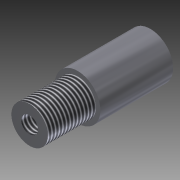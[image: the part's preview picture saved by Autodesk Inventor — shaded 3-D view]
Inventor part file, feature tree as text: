
AUTODESK INVENTOR PART (.ipt)
format: ipt  version: 2012 (Build 160160000, 160)  size: 96,768 bytes
history: native  units: in
note: dims shown in document units (in); Inventor stores cm internally (conversion verified against a paired STEP export)
features: extrude x3, sketch x2, thread x2
ambient origin geometry x8: Origin, YZ Plane, XZ Plane, XY Plane, X Axis, Y Axis, Z Axis, Center Point
bodies: Solid1 (feature_tree)
feature tree (7):
  sketch  "Sketch1"  dims[d0=0.625in d1=0.5in]
  extrude  "Extrusion1"  Depth=0.5in
  extrude  "Extrusion2"  Depth=0.66in TaperAngle=0.0deg
  thread  "Thread1"  [1 undecoded]
  extrude  "Extrusion3"  Depth=0.23in
  thread  "Thread2"  [1 undecoded]
  sketch  "Sketch2"  dims[d2=1.0in d3=0.0in d4=0.66in d5=0.0in d6=1.0in d7=0.0in d8=0.23in d9=1.0in d10=0.0in d11=1.0in d12=0.0in]
note: 2 required parameter values undecoded (feature->parameter linkage not recoverable at this tier; creation-order binding heuristic only, values carry confidence <= 0.55)
